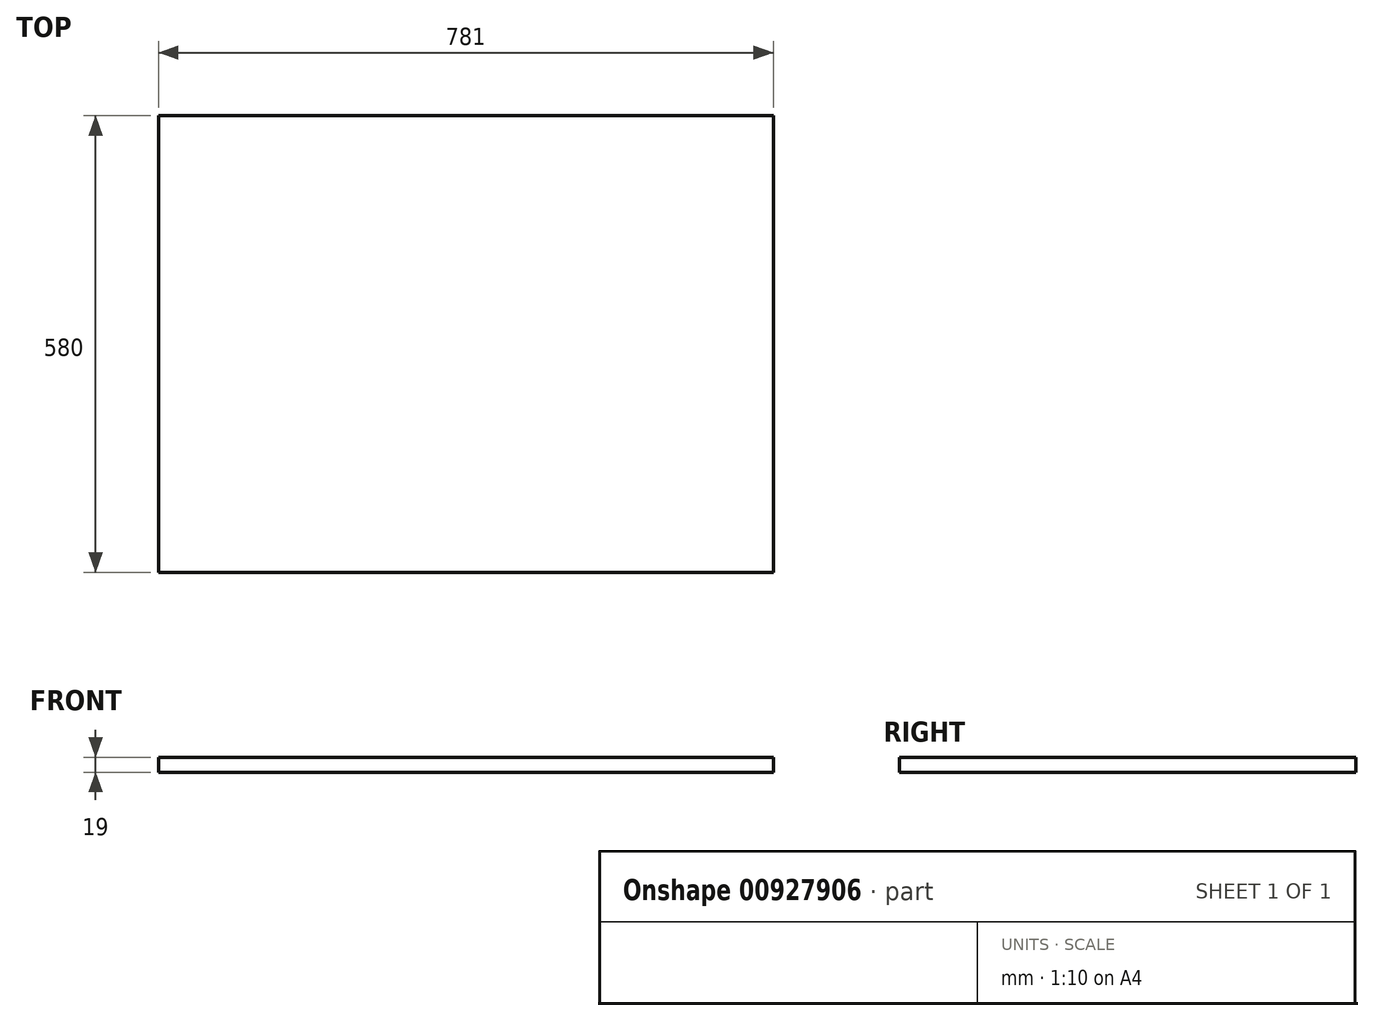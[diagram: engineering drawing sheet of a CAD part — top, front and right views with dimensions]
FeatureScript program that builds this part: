
annotation { "Feature Type Name" : "Feature", "Feature Type Description" : "" }
export const myFeature = defineFeature(function(context is Context, id is Id, definition is map)
    precondition{}
    {
        {
            var Q0;
            Q0=qCreatedBy(makeId("Top.planeOp"),FACE);
            var sketch = newSketch(context, id + "F0", { "sketchPlane" : qUnion([Q0])});
            skLineSegment(sketch, "E0.bottom", {"start": v(0, 0) * mm, "end": v(781, 0) * mm});
            skLineSegment(sketch, "E0.top", {"start": v(0, 580) * mm, "end": v(781, 580) * mm});
            skLineSegment(sketch, "E0.left", {"start": v(0, 0) * mm, "end": v(0, 580) * mm});
            skLineSegment(sketch, "E0.right", {"start": v(781, 0) * mm, "end": v(781, 580) * mm});
            skSolve(sketch);
        }
        {
            var Q0;
            Q0=makeQuery(id+"F0.imprint","IMPRINT",FACE,{"disambiguationData":[TD([[makeQuery(id+"F0.imprint","IMPRINT",EDGE,{"derivedFrom":sQuery(id+"F0.wireOp",EDGE,"E0.bottom")}),1.0]])]});
            extrude(context, id + "F1", {"entities" : qUnion([Q0]), "depth" : 19 * mm, "offsetDistance" : 25 * mm});
        }
    });
